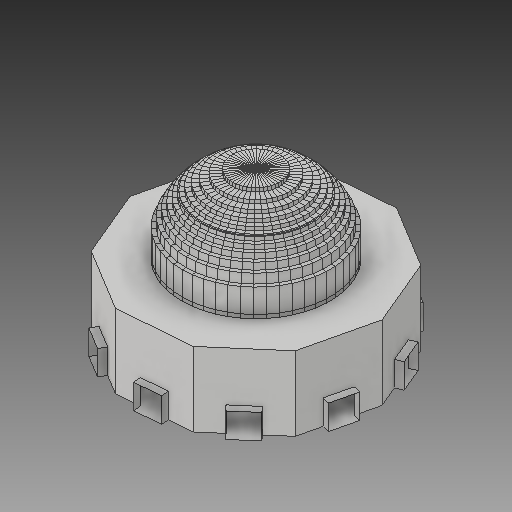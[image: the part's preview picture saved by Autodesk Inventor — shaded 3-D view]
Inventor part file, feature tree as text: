
AUTODESK INVENTOR PART (.ipt)
format: ipt  version: 2017 (Build 210142000, 142)  size: 2,006,016 bytes
history: native  units: in
note: dims shown in document units (in); Inventor stores cm internally (conversion verified against a paired STEP export)
features: extrude x8, sketch x7, other x3, pattern_circular x2, plane x1
ambient origin geometry x8: Origin, YZ Plane, XZ Plane, XY Plane, X Axis, Y Axis, Z Axis, Center Point
bodies: Solid1 (feature_tree)
feature tree (21):
  extrude  "bace"  Depth=1.0in TaperAngle=0.0deg
  extrude  "bace wall"  Depth=1.0in TaperAngle=0.0deg
  extrude  "bace ceiling"  Depth=1.0in
  other  "used to find the workplane for the dome"
  plane  "workplane for dome"
  extrude  "dome make"  Depth=1.0in TaperAngle=0.0deg
  sketch  "Sketch18"  dims[d190=45.0deg d192=1.0in d193=1.0in d194=1.0in d195=1.0in d196=1.0in d197=1.0in d198=1.0in d199=1.0in d200=0.0in d201=1.0in d202=0.0in d204=1.0in d205=19.685in d206=360.0deg d208=1.0in d209=3.937in d210=360.0deg]
  extrude  "dome part cut 1"  Depth=2.5166in TaperAngle=90.0deg
  extrude  "dome part cut 2"  Depth=42.0in
  pattern_circular  "Circular Pattern6"  [2 undecoded]
  extrude  "door frame"  Depth=1.0in
  extrude  "corridor connection"  Depth=1.0in
  pattern_circular  "Circular Pattern of corridor connection"  [2 undecoded]
  other  "Delete Faces of the room"
  other  "Delete Faces of dome"
  sketch  "Sketch1"  dims[d0=62.0in d1=1.0in d2=0.0in]
  sketch  "Sketch2"  dims[d4=1.0in d5=20.0in d6=0.0in]
  sketch  "Sketch3"  dims[d8=1.0in d9=0.0in d16=3.5in d17=6.6667in]
  sketch  "Sketch8"  dims[d18=1.0in d19=0.0in d107=1.0in d108=0.0in]
  sketch  "Sketch12"  dims[d109=40.0in d110=90.0deg d166=2.5166in]
  sketch  "Sketch17"  dims[d186=21.0in d187=0.0in d189=42.0in]
note: 4 required parameter values undecoded (feature->parameter linkage not recoverable at this tier; creation-order binding heuristic only, values carry confidence <= 0.55)
